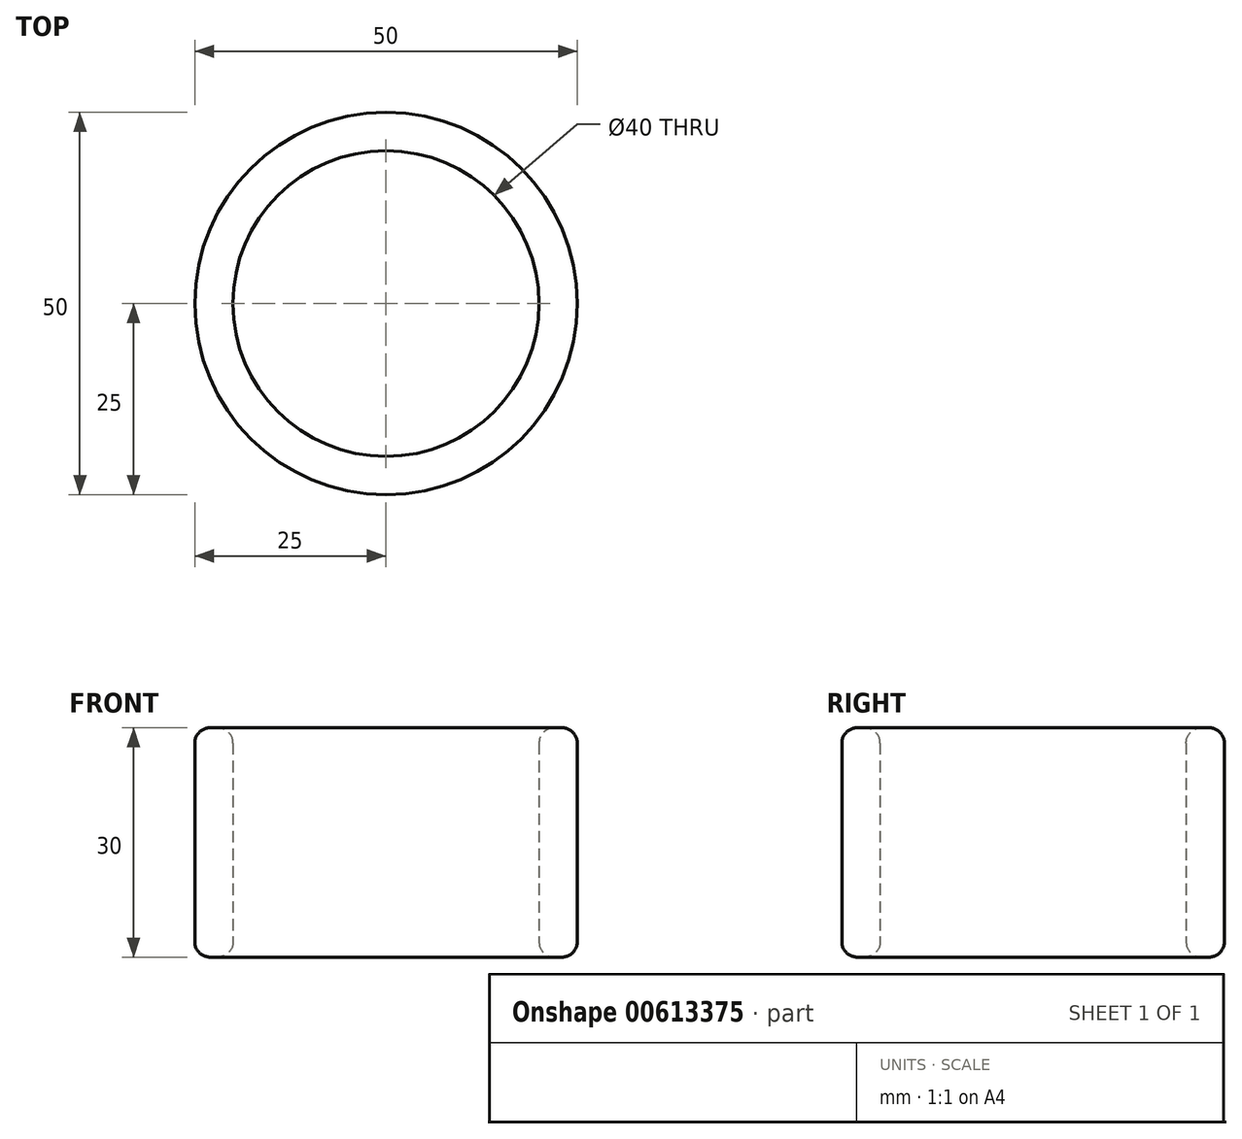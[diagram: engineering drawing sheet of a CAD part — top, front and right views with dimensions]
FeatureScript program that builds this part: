
annotation { "Feature Type Name" : "Feature", "Feature Type Description" : "" }
export const myFeature = defineFeature(function(context is Context, id is Id, definition is map)
    precondition{}
    {
        {
            var Q0;
            Q0=qCreatedBy(makeId("Top.planeOp"),FACE);
            var sketch = newSketch(context, id + "F0", { "sketchPlane" : qUnion([Q0])});
            skCircle(sketch, "E0", {"center": v(0, 0) * mm, "radius": 20 * mm});
            skCircle(sketch, "E1", {"center": v(0, 0) * mm, "radius": 25 * mm});
            skSolve(sketch);
        }
        {
            var Q0;
            Q0=makeQuery(id+"F0.imprint","IMPRINT",FACE,{"disambiguationData":[TD([[makeQuery(id+"F0.imprint","IMPRINT",EDGE,{"derivedFrom":sQuery(id+"F0.wireOp",EDGE,"E0")}),-1.0]])]});
            var Q1;
            Q1=sQuery(id+"F0.wireOp",EDGE,"E1");
            var Q2;
            Q2=sQuery(id+"F0.wireOp",EDGE,"E0");
            extrude(context, id + "F1", {"entities" : qUnion([Q0]), "surfaceEntities" : qUnion([Q1, Q2]), "depth" : 30 * mm, "offsetDistance" : 25 * mm});
        }
        {
            var Q0;
            Q0=makeQuery(id+"F1.opExtrude","CAP_EDGE",EDGE,{"disambiguationData":[OSD([sQuery(id+"F0.wireOp",EDGE,"E0")])],"isStart":false});
            var Q1;
            Q1=makeQuery(id+"F1.opExtrude","CAP_EDGE",EDGE,{"disambiguationData":[OSD([sQuery(id+"F0.wireOp",EDGE,"E0")])],"isStart":true});
            var Q2;
            Q2=makeQuery(id+"F1.opExtrude","CAP_EDGE",EDGE,{"disambiguationData":[OSD([sQuery(id+"F0.wireOp",EDGE,"E1")])],"isStart":false});
            var Q3;
            Q3=makeQuery(id+"F1.opExtrude","CAP_EDGE",EDGE,{"disambiguationData":[OSD([sQuery(id+"F0.wireOp",EDGE,"E1")])],"isStart":true});
            fillet(context, id + "F2", {"entities" : qUnion([Q0, Q1, Q2, Q3]), "radius" : 2 * mm, "tangentPropagation" : true, "allowEdgeOverflow" : false});
        }
    });
